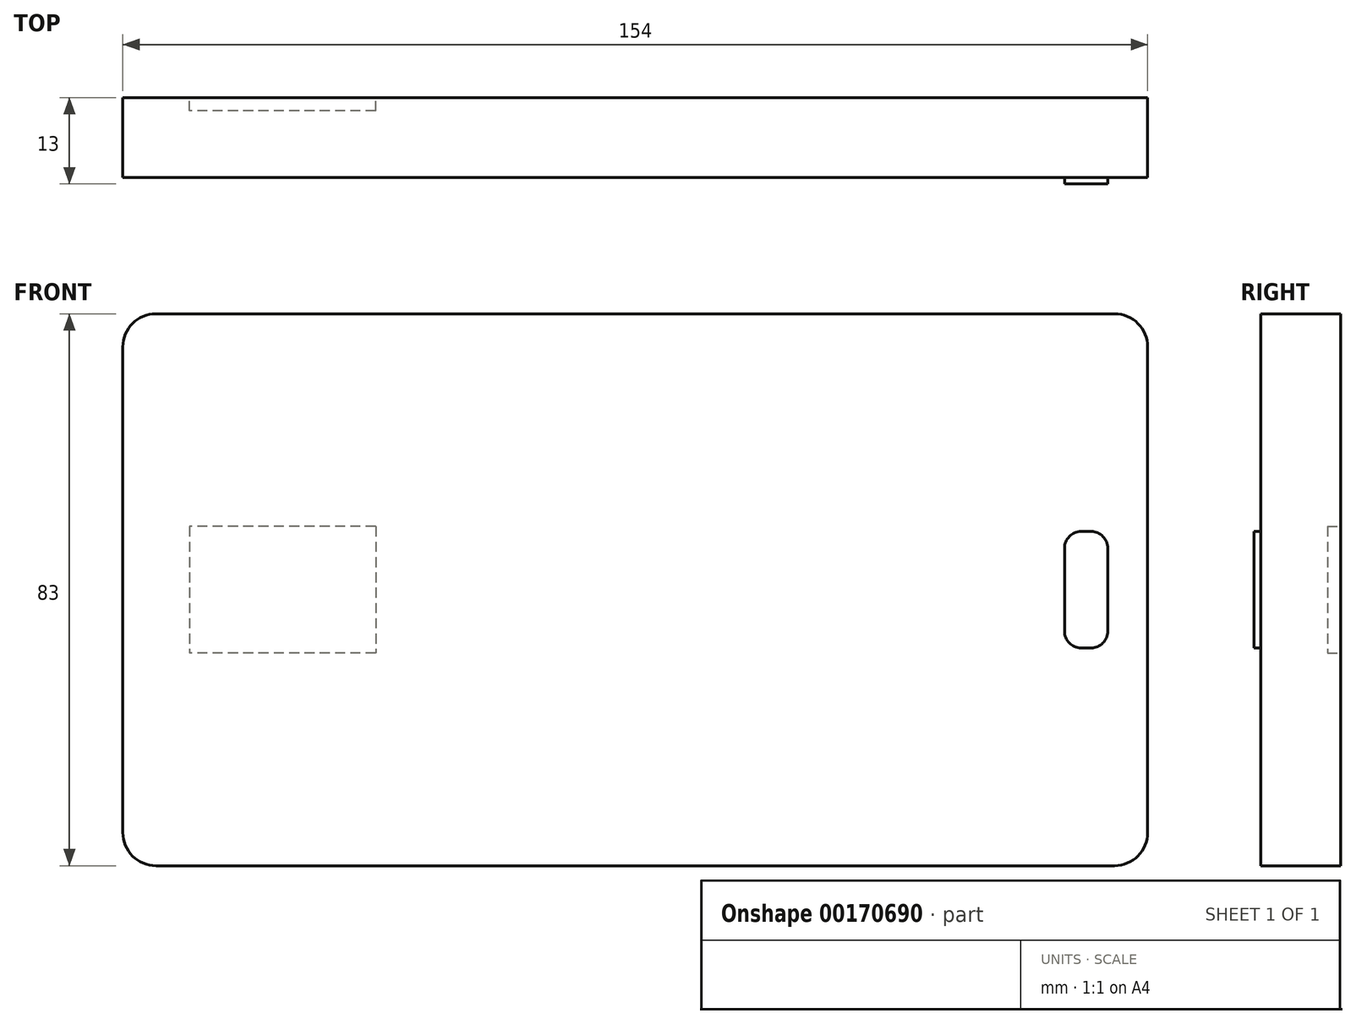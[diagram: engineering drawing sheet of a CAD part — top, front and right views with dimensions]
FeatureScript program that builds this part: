
annotation { "Feature Type Name" : "Feature", "Feature Type Description" : "" }
export const myFeature = defineFeature(function(context is Context, id is Id, definition is map)
    precondition{}
    {
        {
            var Q0;
            Q0=qCreatedBy(makeId("Front.planeOp"),FACE);
            var sketch = newSketch(context, id + "F0", { "sketchPlane" : qUnion([Q0])});
            skLineSegment(sketch, "E0.bottom", {"start": v(77, 41.5) * mm, "end": v(-77, 41.5) * mm});
            skLineSegment(sketch, "E0.top", {"start": v(77, -41.5) * mm, "end": v(-77, -41.5) * mm});
            skLineSegment(sketch, "E0.left", {"start": v(77, 41.5) * mm, "end": v(77, -41.5) * mm});
            skLineSegment(sketch, "E0.right", {"start": v(-77, 41.5) * mm, "end": v(-77, -41.5) * mm});
            skPoint(sketch, "E0.middle", {"position": v(0, 0) * mm});
            skSolve(sketch);
        }
        {
            var Q0;
            Q0=makeQuery(id+"F0.imprint","IMPRINT",FACE,{"disambiguationData":[TD([[makeQuery(id+"F0.imprint","IMPRINT",EDGE,{"derivedFrom":sQuery(id+"F0.wireOp",EDGE,"E0.bottom")}),1.0]])]});
            extrude(context, id + "F1", {"entities" : qUnion([Q0]), "depth" : 12 * mm});
        }
        {
            var Q0;
            Q0=makeQuery(id+"F1.opExtrude","SWEPT_EDGE",EDGE,{"disambiguationData":[OSD([sQuery(id+"F0.wireOp",EDGE,"E0.bottom"),sQuery(id+"F0.wireOp",EDGE,"E0.right")])]});
            var Q1;
            Q1=makeQuery(id+"F1.opExtrude","SWEPT_EDGE",EDGE,{"disambiguationData":[OSD([sQuery(id+"F0.wireOp",EDGE,"E0.bottom"),sQuery(id+"F0.wireOp",EDGE,"E0.left")])]});
            var Q2;
            Q2=makeQuery(id+"F1.opExtrude","SWEPT_EDGE",EDGE,{"disambiguationData":[OSD([sQuery(id+"F0.wireOp",EDGE,"E0.top"),sQuery(id+"F0.wireOp",EDGE,"E0.left")])]});
            var Q3;
            Q3=makeQuery(id+"F1.opExtrude","SWEPT_EDGE",EDGE,{"disambiguationData":[OSD([sQuery(id+"F0.wireOp",EDGE,"E0.top"),sQuery(id+"F0.wireOp",EDGE,"E0.right")])]});
            fillet(context, id + "F2", {"entities" : qUnion([Q0, Q1, Q2, Q3]), "radius" : 5 * mm, "tangentPropagation" : true, "allowEdgeOverflow" : false});
        }
        {
            var Q0;
            Q0=makeQuery(id+"F1.opExtrude","CAP_FACE",FACE,{"disambiguationData":[OSD([sQuery(id+"F0.wireOp",EDGE,"E0.bottom"),sQuery(id+"F0.wireOp",EDGE,"E0.top"),sQuery(id+"F0.wireOp",EDGE,"E0.left"),sQuery(id+"F0.wireOp",EDGE,"E0.right")])],"isStart":false});
            var sketch = newSketch(context, id + "F3", { "sketchPlane" : qUnion([Q0])});
            skLineSegment(sketch, "E1.bottom", {"start": v(64.5, 8.75) * mm, "end": v(71, 8.75) * mm});
            skLineSegment(sketch, "E1.top", {"start": v(64.5, -8.75) * mm, "end": v(71, -8.75) * mm});
            skLineSegment(sketch, "E1.left", {"start": v(64.5, 8.75) * mm, "end": v(64.5, -8.75) * mm});
            skLineSegment(sketch, "E1.right", {"start": v(71, 8.75) * mm, "end": v(71, -8.75) * mm});
            skPoint(sketch, "E1.middle", {"position": v(67.75, 0) * mm});
            skSolve(sketch);
        }
        {
            var Q0;
            Q0=makeQuery(id+"F3.imprint","IMPRINT",FACE,{"disambiguationData":[TD([[makeQuery(id+"F3.imprint","IMPRINT",EDGE,{"derivedFrom":sQuery(id+"F3.wireOp",EDGE,"E1.bottom")}),-1.0]])]});
            extrude(context, id + "F4", {"entities" : qUnion([Q0]), "operationType" : NewBodyOperationType.ADD, "depth" : 1 * mm});
        }
        {
            var Q0;
            Q0=makeQuery(id+"F4.opExtrude","SWEPT_EDGE",EDGE,{"disambiguationData":[OSD([sQuery(id+"F3.wireOp",EDGE,"E1.top"),sQuery(id+"F3.wireOp",EDGE,"E1.right")])]});
            var Q1;
            Q1=makeQuery(id+"F4.opExtrude","SWEPT_EDGE",EDGE,{"disambiguationData":[OSD([sQuery(id+"F3.wireOp",EDGE,"E1.bottom"),sQuery(id+"F3.wireOp",EDGE,"E1.right")])]});
            var Q2;
            Q2=makeQuery(id+"F4.opExtrude","SWEPT_EDGE",EDGE,{"disambiguationData":[OSD([sQuery(id+"F3.wireOp",EDGE,"E1.bottom"),sQuery(id+"F3.wireOp",EDGE,"E1.left")])]});
            var Q3;
            Q3=makeQuery(id+"F4.opExtrude","SWEPT_EDGE",EDGE,{"disambiguationData":[OSD([sQuery(id+"F3.wireOp",EDGE,"E1.top"),sQuery(id+"F3.wireOp",EDGE,"E1.left")])]});
            fillet(context, id + "F5", {"entities" : qUnion([Q0, Q1, Q2, Q3]), "radius" : 2.5 * mm, "tangentPropagation" : true, "allowEdgeOverflow" : false});
        }
        {
            var Q0;
            Q0=qCreatedBy(makeId("Front.planeOp"),FACE);
            var sketch = newSketch(context, id + "F6", { "sketchPlane" : qUnion([Q0])});
            skLineSegment(sketch, "E2.bottom", {"start": v(-39, 9.5) * mm, "end": v(-67, 9.5) * mm});
            skLineSegment(sketch, "E2.top", {"start": v(-39, -9.5) * mm, "end": v(-67, -9.5) * mm});
            skLineSegment(sketch, "E2.left", {"start": v(-39, 9.5) * mm, "end": v(-39, -9.5) * mm});
            skLineSegment(sketch, "E2.right", {"start": v(-67, 9.5) * mm, "end": v(-67, -9.5) * mm});
            skSolve(sketch);
        }
        {
            var Q0;
            Q0=makeQuery(id+"F6.imprint","IMPRINT",FACE,{"disambiguationData":[TD([[makeQuery(id+"F6.imprint","IMPRINT",EDGE,{"derivedFrom":sQuery(id+"F6.wireOp",EDGE,"E2.bottom")}),1.0]])]});
            extrude(context, id + "F7", {"entities" : qUnion([Q0]), "operationType" : NewBodyOperationType.REMOVE, "depth" : 2 * mm});
        }
    });
